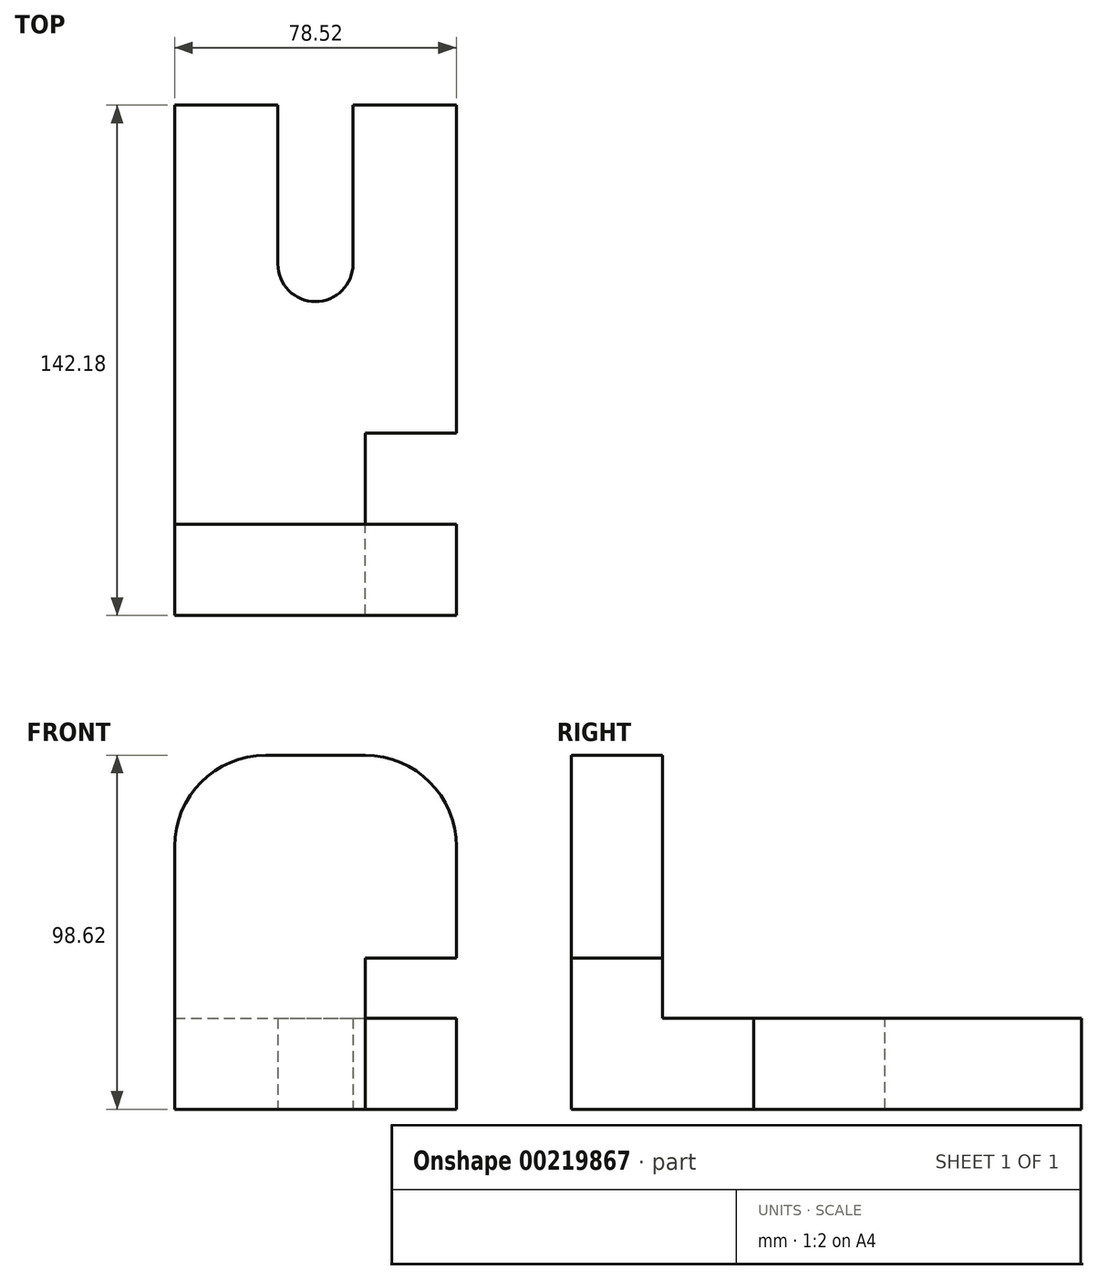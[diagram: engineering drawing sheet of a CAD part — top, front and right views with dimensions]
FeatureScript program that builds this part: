
annotation { "Feature Type Name" : "Feature", "Feature Type Description" : "" }
export const myFeature = defineFeature(function(context is Context, id is Id, definition is map)
    precondition{}
    {
        {
            var Q0;
            Q0=qCreatedBy(makeId("Top.planeOp"),FACE);
            var sketch = newSketch(context, id + "F0", { "sketchPlane" : qUnion([Q0])});
            skLineSegment(sketch, "E0.bottom", {"start": v(-39.26, 58.4) * mm, "end": v(39.26, 58.4) * mm});
            skLineSegment(sketch, "E0.top", {"start": v(-39.26, -58.4) * mm, "end": v(39.26, -58.4) * mm});
            skLineSegment(sketch, "E0.left", {"start": v(-39.26, 58.4) * mm, "end": v(-39.26, -58.4) * mm});
            skLineSegment(sketch, "E0.right", {"start": v(39.26, 58.4) * mm, "end": v(39.26, -58.4) * mm});
            skPoint(sketch, "E0.middle", {"position": v(0, 0) * mm});
            skSolve(sketch);
        }
        {
            var Q0;
            Q0=makeQuery(id+"F0.imprint","IMPRINT",FACE,{"disambiguationData":[TD([[makeQuery(id+"F0.imprint","IMPRINT",EDGE,{"derivedFrom":sQuery(id+"F0.wireOp",EDGE,"E0.bottom")}),-1.0]])]});
            extrude(context, id + "F1", {"entities" : qUnion([Q0]), "depth" : 25.4 * mm});
        }
        {
            var Q0;
            Q0=makeQuery(id+"F1.opExtrude","CAP_FACE",FACE,{"disambiguationData":[OSD([sQuery(id+"F0.wireOp",EDGE,"E0.bottom"),sQuery(id+"F0.wireOp",EDGE,"E0.top"),sQuery(id+"F0.wireOp",EDGE,"E0.left"),sQuery(id+"F0.wireOp",EDGE,"E0.right")])],"isStart":false});
            var sketch = newSketch(context, id + "F2", { "sketchPlane" : qUnion([Q0])});
            skLineSegment(sketch, "E1.bottom", {"start": v(-10.46, 14.12) * mm, "end": v(10.46, 14.12) * mm});
            skLineSegment(sketch, "E1.top", {"start": v(-10.46, 102.67) * mm, "end": v(10.46, 102.67) * mm});
            skLineSegment(sketch, "E1.left", {"start": v(-10.46, 14.12) * mm, "end": v(-10.46, 102.67) * mm});
            skLineSegment(sketch, "E1.right", {"start": v(10.46, 14.12) * mm, "end": v(10.46, 102.67) * mm});
            skPoint(sketch, "E1.middle", {"position": v(0, 58.4) * mm});
            skSolve(sketch);
        }
        {
            var Q0;
            Q0 = qSketchRegion(id + "F2", true);
            extrude(context, id + "F3", {"entities" : qUnion([Q0]), "operationType" : NewBodyOperationType.REMOVE, "endBound" : BoundingType.THROUGH_ALL, "oppositeDirection" : true, "depth" : 25.4 * mm});
        }
        {
            var Q0;
            Q0=makeQuery(id+"F1.opExtrude","CAP_FACE",FACE,{"disambiguationData":[OSD([sQuery(id+"F0.wireOp",EDGE,"E0.bottom"),sQuery(id+"F0.wireOp",EDGE,"E0.top"),sQuery(id+"F0.wireOp",EDGE,"E0.left"),sQuery(id+"F0.wireOp",EDGE,"E0.right")])],"isStart":false});
            var sketch = newSketch(context, id + "F4", { "sketchPlane" : qUnion([Q0])});
            skCircle(sketch, "E2", {"center": v(0, 14.12) * mm, "radius": 10.46 * mm});
            skSolve(sketch);
        }
        {
            var Q0;
            Q0 = qSketchRegion(id + "F4", true);
            extrude(context, id + "F5", {"entities" : qUnion([Q0]), "operationType" : NewBodyOperationType.REMOVE, "oppositeDirection" : true, "depth" : 25.4 * mm});
        }
        {
            var Q0;
            Q0=makeQuery(id+"F1.opExtrude","SWEPT_FACE",FACE,{"disambiguationData":[OSD([sQuery(id+"F0.wireOp",EDGE,"E0.top")])]});
            var sketch = newSketch(context, id + "F6", { "sketchPlane" : qUnion([Q0])});
            skPoint(sketch, "E3.oppositeSnap0", {"position": v(39.26, 12.7) * mm});
            skLineSegment(sketch, "E3.bottom", {"start": v(-39.26, 0) * mm, "end": v(39.26, 0) * mm});
            skLineSegment(sketch, "E3.top", {"start": v(-39.26, 98.62) * mm, "end": v(39.26, 98.62) * mm});
            skLineSegment(sketch, "E3.left", {"start": v(-39.26, 0) * mm, "end": v(-39.26, 98.62) * mm});
            skLineSegment(sketch, "E3.right", {"start": v(39.26, 0) * mm, "end": v(39.26, 98.62) * mm});
            skSolve(sketch);
        }
        {
            var Q0;
            Q0 = qSketchRegion(id + "F6", true);
            extrude(context, id + "F7", {"entities" : qUnion([Q0]), "operationType" : NewBodyOperationType.ADD, "depth" : 25.4 * mm});
        }
        {
            var Q0;
            Q0=makeQuery(id+"F7.opExtrude","SWEPT_EDGE",EDGE,{"disambiguationData":[OSD([sQuery(id+"F6.wireOp",EDGE,"E3.top"),sQuery(id+"F6.wireOp",EDGE,"E3.left")])]});
            var Q1;
            Q1=makeQuery(id+"F7.opExtrude","SWEPT_EDGE",EDGE,{"disambiguationData":[OSD([sQuery(id+"F6.wireOp",EDGE,"E3.top"),sQuery(id+"F6.wireOp",EDGE,"E3.right")])]});
            fillet(context, id + "F8", {"entities" : qUnion([Q0, Q1]), "radius" : 25.4 * mm, "tangentPropagation" : true, "allowEdgeOverflow" : false});
        }
        {
            var Q0;
            Q0=makeQuery(id+"F7.boolean.opBoolean","MERGE",FACE,{"derivedFrom":[makeQuery(id+"F1.opExtrude","SWEPT_FACE",FACE,{"disambiguationData":[OSD([sQuery(id+"F0.wireOp",EDGE,"E0.right")])]}),makeQuery(id+"F7.opExtrude","SWEPT_FACE",FACE,{"disambiguationData":[OSD([sQuery(id+"F6.wireOp",EDGE,"E3.right")])]})]});
            var sketch = newSketch(context, id + "F9", { "sketchPlane" : qUnion([Q0])});
            skLineSegment(sketch, "E4.bottom", {"start": v(-83.8, 0) * mm, "end": v(-58.4, 0) * mm});
            skLineSegment(sketch, "E4.top", {"start": v(-83.8, 42.1) * mm, "end": v(-58.4, 42.1) * mm});
            skLineSegment(sketch, "E4.left", {"start": v(-83.8, 0) * mm, "end": v(-83.8, 42.1) * mm});
            skLineSegment(sketch, "E4.right", {"start": v(-58.4, 0) * mm, "end": v(-58.4, 42.1) * mm});
            skSolve(sketch);
        }
        {
            var Q0;
            Q0 = qSketchRegion(id + "F9", true);
            extrude(context, id + "F10", {"entities" : qUnion([Q0]), "operationType" : NewBodyOperationType.REMOVE, "oppositeDirection" : true, "depth" : 25.4 * mm});
        }
        {
            var Q0;
            Q0=makeQuery(id+"F10.boolean.opBoolean","COPY",FACE,{"derivedFrom":makeQuery(id+"F10.opExtrude","SWEPT_FACE",FACE,{"disambiguationData":[OSD([sQuery(id+"F9.wireOp",EDGE,"E4.right")])]})});
            extrude(context, id + "F11", {"entities" : qUnion([Q0]), "operationType" : NewBodyOperationType.REMOVE, "oppositeDirection" : true, "depth" : 25.4 * mm});
        }
    });
